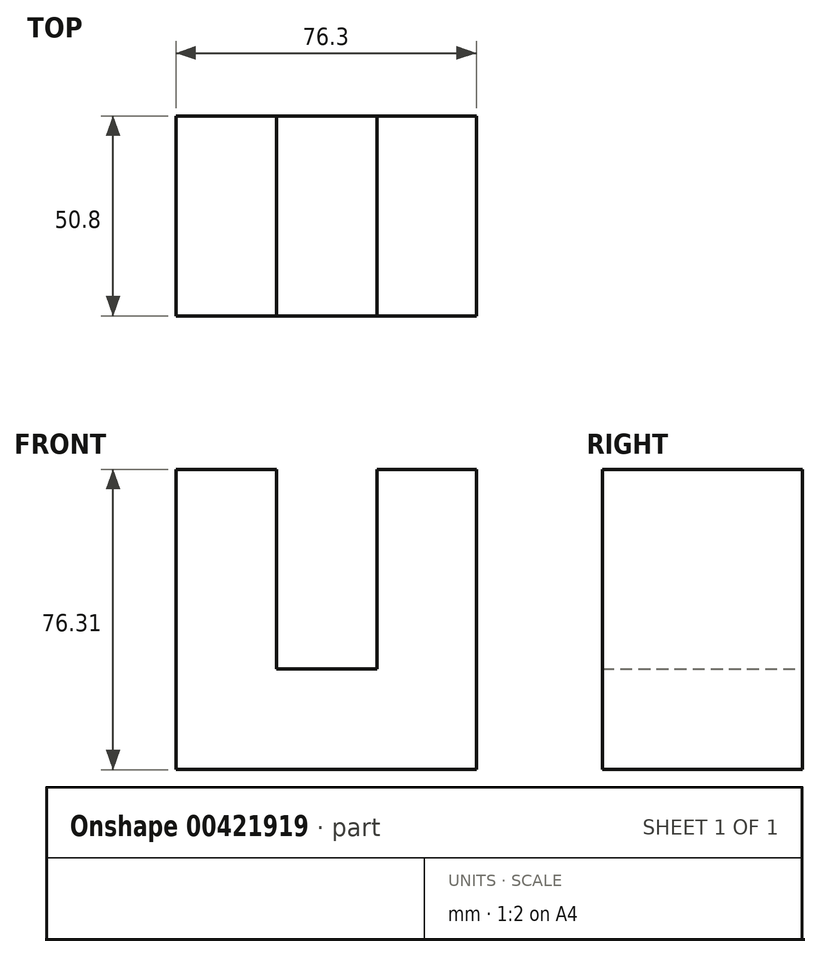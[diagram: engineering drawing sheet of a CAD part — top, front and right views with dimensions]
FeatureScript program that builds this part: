
annotation { "Feature Type Name" : "Feature", "Feature Type Description" : "" }
export const myFeature = defineFeature(function(context is Context, id is Id, definition is map)
    precondition{}
    {
        {
            var Q0;
            Q0=qCreatedBy(makeId("Front.planeOp"),FACE);
            var sketch = newSketch(context, id + "F0", { "sketchPlane" : qUnion([Q0])});
            skPoint(sketch, "E0.start.orphan", {"position": v(49.4, 0) * mm});
            skLineSegment(sketch, "E1", {"start": v(-34.58, -31.7) * mm, "end": v(41.72, -31.7) * mm});
            skLineSegment(sketch, "E2", {"start": v(41.72, -31.7) * mm, "end": v(41.72, 44.6) * mm});
            skLineSegment(sketch, "E3", {"start": v(-34.58, -31.7) * mm, "end": v(-34.58, 44.6) * mm});
            skLineSegment(sketch, "E4", {"start": v(-34.58, 44.6) * mm, "end": v(-9.06, 44.6) * mm});
            skLineSegment(sketch, "E5", {"start": v(41.72, 44.6) * mm, "end": v(16.47, 44.6) * mm});
            skLineSegment(sketch, "E6", {"start": v(16.47, 44.6) * mm, "end": v(16.47, -6.18) * mm});
            skLineSegment(sketch, "E7", {"start": v(-9.06, 44.6) * mm, "end": v(-9.06, -6.18) * mm});
            skLineSegment(sketch, "E8", {"start": v(-9.06, -6.18) * mm, "end": v(16.47, -6.18) * mm});
            skSolve(sketch);
        }
        {
            var Q0;
            Q0 = qSketchRegion(id + "F0", true);
            extrude(context, id + "F1", {"entities" : qUnion([Q0]), "depth" : 50.8 * mm});
        }
    });
